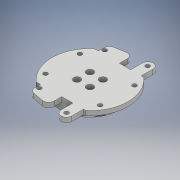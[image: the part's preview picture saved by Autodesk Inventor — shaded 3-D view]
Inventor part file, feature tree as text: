
AUTODESK INVENTOR PART (.ipt)
format: ipt  version: 2017 (Build 210142000, 142)  size: 564,736 bytes
history: native  units: mm
features: reference x4, other x3, sketch x2, plane x2, mirror x2, hole x1, extrude x1
ambient origin geometry x8: Origin, YZ Plane, XZ Plane, XY Plane, X Axis, Y Axis, Z Axis, Center Point
bodies: Solid1 (feature_tree)
feature tree (15):
  other  "Arm - swing base.ipt"
  sketch  "Sketch2"  dims[d0=10.0mm]
  hole  "Hole1"  [1 undecoded]
  extrude  "Extrusion1"  Depth=7.2mm
  plane  "Work Plane1"
  mirror  "Mirror1"
  plane  "Work Plane2"
  mirror  "Mirror2"
  other  "Base Plate::Arm - swing base.ipt"
  other  "TaggingFeature1"
  reference  "Reference1"
  reference  "Reference2"
  reference  "Reference3"
  reference  "Reference4"
  sketch  "Sketch3"  dims[d1=4.3mm d2=6.0mm d3=8.0mm d4=4.0mm d5=90.0deg d6=8.0mm d7=20.594885mm d9=7.2mm d10=7.2mm d11=6.0mm d12=0.0mm]
note: 1 required parameter value undecoded (feature->parameter linkage not recoverable at this tier; creation-order binding heuristic only, values carry confidence <= 0.55)
